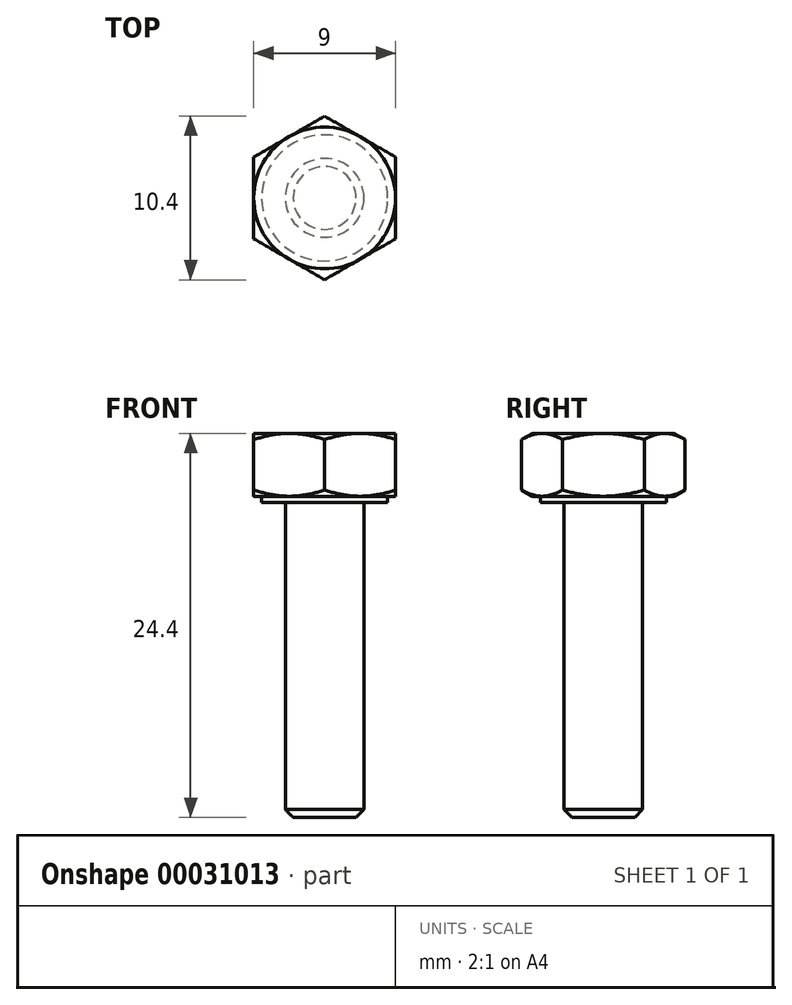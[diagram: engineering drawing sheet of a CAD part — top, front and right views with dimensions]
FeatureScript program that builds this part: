
annotation { "Feature Type Name" : "Feature", "Feature Type Description" : "" }
export const myFeature = defineFeature(function(context is Context, id is Id, definition is map)
    precondition{}
    {
        {
            var Q0;
            Q0=qCreatedBy(makeId("Front.planeOp"),FACE);
            var sketch = newSketch(context, id + "F0", { "sketchPlane" : qUnion([Q0])});
            skLineSegment(sketch, "E0.bottom", {"start": v(0, 0) * mm, "end": v(2.5, 0) * mm});
            skLineSegment(sketch, "E0.left", {"start": v(0, 0) * mm, "end": v(0, 20.4) * mm});
            skLineSegment(sketch, "E0.right", {"start": v(2.5, 0) * mm, "end": v(2.5, 20) * mm});
            skLineSegment(sketch, "E1.bottom", {"start": v(2.5, 20) * mm, "end": v(4, 20) * mm});
            skLineSegment(sketch, "E1.top", {"start": v(0, 20.4) * mm, "end": v(4, 20.4) * mm});
            skLineSegment(sketch, "E1.right", {"start": v(4, 20) * mm, "end": v(4, 20.4) * mm});
            skSolve(sketch);
        }
        {
            var Q0;
            Q0=qSketchRegion(id+"F0",true);
            var Q1;
            Q1=sQuery(id+"F0.wireOp",EDGE,"E0.left");
            revolve(context, id + "F1", {"entities" : qUnion([Q0]), "axis" : qUnion([Q1]), "revolveType" : RevolveType.FULL});
        }
        {
            var Q0;
            Q0=makeQuery(id+"F1.opRevolve","SWEPT_FACE",FACE,{"disambiguationData":[OSD([sQuery(id+"F0.wireOp",EDGE,"E1.top")])]});
            var sketch = newSketch(context, id + "F2", { "sketchPlane" : qUnion([Q0])});
            skCircle(sketch, "E2", {"center": v(0, 0) * mm, "radius": 4.5 * mm});
            skCircle(sketch, "E3.cCircle", {"center": v(0, 0) * mm, "radius": 4.5 * mm, "construction": true});
            skLineSegment(sketch, "E3.0", {"start": v(4.5, 2.6) * mm, "end": v(4.5, -2.6) * mm});
            skLineSegment(sketch, "E3.1", {"start": v(4.5, -2.6) * mm, "end": v(0, -5.2) * mm});
            skLineSegment(sketch, "E3.2", {"start": v(0, -5.2) * mm, "end": v(-4.5, -2.6) * mm});
            skLineSegment(sketch, "E3.3", {"start": v(-4.5, -2.6) * mm, "end": v(-4.5, 2.6) * mm});
            skLineSegment(sketch, "E3.4", {"start": v(-4.5, 2.6) * mm, "end": v(0, 5.2) * mm});
            skLineSegment(sketch, "E3.5", {"start": v(0, 5.2) * mm, "end": v(4.5, 2.6) * mm});
            skPoint(sketch, "E3.0.midPoint", {"position": v(4.5, 0) * mm});
            skSolve(sketch);
        }
        {
            var Q0;
            Q0=qSketchRegion(id+"F2",true);
            extrude(context, id + "F3", {"entities" : qUnion([Q0]), "operationType" : NewBodyOperationType.ADD, "depth" : 4 * mm});
        }
        {
            var Q0;
            Q0=qCreatedBy(makeId("Front.planeOp"),FACE);
            var sketch = newSketch(context, id + "F4", { "sketchPlane" : qUnion([Q0])});
            skLineSegment(sketch, "E4", {"start": v(0, 24.4) * mm, "end": v(0, 20.4) * mm, "construction": true});
            skLineSegment(sketch, "E5", {"start": v(0, 22.4) * mm, "end": v(-4.5, 22.4) * mm, "construction": true});
            skLineSegment(sketch, "E6", {"start": v(-4.5, 24.4) * mm, "end": v(-9.88, 24.4) * mm});
            skLineSegment(sketch, "E7", {"start": v(-9.88, 24.4) * mm, "end": v(-9.88, 21.3) * mm});
            skLineSegment(sketch, "E8", {"start": v(-9.88, 21.3) * mm, "end": v(-4.5, 24.4) * mm});
            skLineSegment(sketch, "E9.0.MirrorCS", {"start": v(-9.88, 23.5) * mm, "end": v(-4.5, 20.4) * mm});
            skLineSegment(sketch, "E9.1.MirrorCS", {"start": v(-4.5, 20.4) * mm, "end": v(-9.88, 20.4) * mm});
            skLineSegment(sketch, "E9.2.MirrorCS", {"start": v(-9.88, 20.4) * mm, "end": v(-9.88, 23.5) * mm});
            skSolve(sketch);
        }
        {
            var Q0;
            Q0=qSketchRegion(id+"F4",true);
            var Q1;
            Q1=sQuery(id+"F4.wireOp",EDGE,"E4");
            revolve(context, id + "F5", {"operationType" : NewBodyOperationType.REMOVE, "entities" : qUnion([Q0]), "axis" : qUnion([Q1]), "revolveType" : RevolveType.FULL, "oppositeDirection" : true});
        }
        {
            var Q0;
            Q0=makeQuery(id+"F1.opRevolve","SWEPT_EDGE",EDGE,{"disambiguationData":[OSD([sQuery(id+"F0.wireOp",EDGE,"E0.bottom"),sQuery(id+"F0.wireOp",EDGE,"E0.right")])]});
            chamfer(context, id + "F6", {"entities" : qUnion([Q0]), "width" : .5 * mm, "tangentPropagation" : true});
        }
    });
